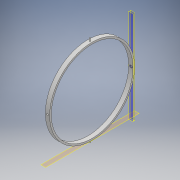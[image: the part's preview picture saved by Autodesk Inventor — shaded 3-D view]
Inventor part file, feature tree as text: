
AUTODESK INVENTOR PART (.ipt)
format: ipt  version: 2018 (Build 220112000, 112)  size: 160,256 bytes
history: native  units: mm
features: extrude x5, sketch x5, plane x3, mirror x2, projected_geometry x1
ambient origin geometry x8: Origin, YZ Plane, XZ Plane, XY Plane, X Axis, Y Axis, Z Axis, Center Point
bodies: Solid1 (feature_tree)
feature tree (16):
  extrude  "Extrusion1"  Depth=192.0mm
  plane  "Work Plane1"
  extrude  "Extrusion2"  Depth=10.0mm
  plane  "Work Plane2"
  extrude  "Extrusion3"  Depth=6.0mm
  mirror  "Mirror1"
  plane  "Work Plane3"
  extrude  "Extrusion4"  Depth=3.0mm
  mirror  "Mirror2"
  extrude  "Extrusion5"  Depth=12.0mm TaperAngle=0.0deg
  sketch  "Sketch1"  dims[d0=200.0mm d1=192.0mm]
  sketch  "Sketch2"  dims[d2=10.0mm d3=0.0mm d4=4.0mm]
  projected_geometry  "Projected Loop1"
  sketch  "Sketch3"  dims[d5=206.5mm d6=0.0mm d7=6.0mm]
  sketch  "Sketch4"  dims[d8=2.5mm d9=0.0mm d10=3.0mm]
  sketch  "Sketch5"  dims[d11=12.0mm d12=0.0mm d13=12.0mm d14=0.0mm]
